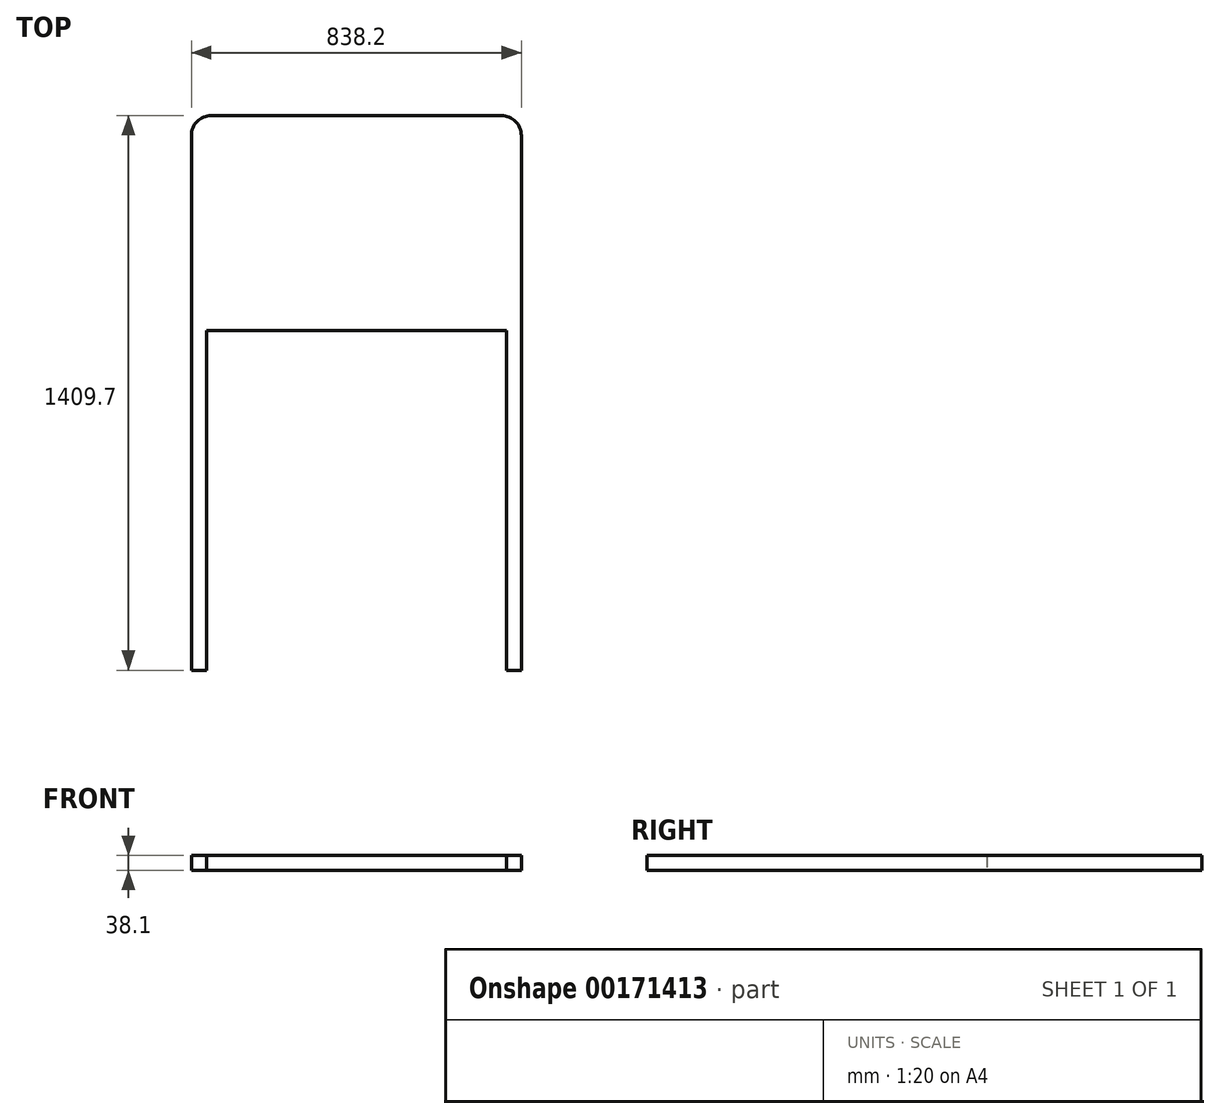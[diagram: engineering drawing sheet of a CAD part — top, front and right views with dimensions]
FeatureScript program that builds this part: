
annotation { "Feature Type Name" : "Feature", "Feature Type Description" : "" }
export const myFeature = defineFeature(function(context is Context, id is Id, definition is map)
    precondition{}
    {
        {
            var Q0;
            Q0=qCreatedBy(makeId("Top.planeOp"),FACE);
            var sketch = newSketch(context, id + "F0", { "sketchPlane" : qUnion([Q0])});
            skLineSegment(sketch, "E0.bottom", {"start": v(-368.3, 704.85) * mm, "end": v(368.3, 704.85) * mm});
            skLineSegment(sketch, "E0.top", {"start": v(-419.1, -704.85) * mm, "end": v(419.1, -704.85) * mm, "construction": true});
            skLineSegment(sketch, "E0.left", {"start": v(-419.1, 654.05) * mm, "end": v(-419.1, -704.85) * mm});
            skLineSegment(sketch, "E0.right", {"start": v(419.1, 654.05) * mm, "end": v(419.1, -704.85) * mm});
            skPoint(sketch, "E0.middle", {"position": v(0, 0) * mm});
            skLineSegment(sketch, "E1", {"start": v(-381, -704.85) * mm, "end": v(-381, 158.75) * mm});
            skLineSegment(sketch, "E2", {"start": v(-381, 158.75) * mm, "end": v(381, 158.75) * mm});
            skLineSegment(sketch, "E3", {"start": v(381, 158.75) * mm, "end": v(381, -704.85) * mm});
            skLineSegment(sketch, "E4", {"start": v(-419.1, -704.85) * mm, "end": v(-381, -704.85) * mm});
            skLineSegment(sketch, "E5", {"start": v(381, -704.85) * mm, "end": v(419.1, -704.85) * mm});
            skPoint(sketch, "E6.visualSharp", {"position": v(419.1, 704.85) * mm});
            skArc(sketch, "E6.filletArc", {"start": v(419.1, 654.05) * mm, "mid": v(404.22, 689.97) * mm, "end": v(368.3, 704.85) * mm});
            skPoint(sketch, "E7.visualSharp", {"position": v(-419.1, 704.85) * mm});
            skArc(sketch, "E7.filletArc", {"start": v(-368.3, 704.85) * mm, "mid": v(-404.22, 689.97) * mm, "end": v(-419.1, 654.05) * mm});
            skSolve(sketch);
        }
        {
            var Q0;
            Q0=makeQuery(id+"F0.imprint","IMPRINT",FACE,{"disambiguationData":[TD([[makeQuery(id+"F0.imprint","IMPRINT",EDGE,{"derivedFrom":sQuery(id+"F0.wireOp",EDGE,"E0.bottom")}),-1.0]])]});
            extrude(context, id + "F1", {"entities" : qUnion([Q0]), "depth" : 38.1 * mm});
        }
    });
